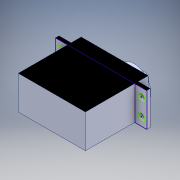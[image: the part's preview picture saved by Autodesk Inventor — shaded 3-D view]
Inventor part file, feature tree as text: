
AUTODESK INVENTOR PART (.ipt)
format: ipt  version: 2018 (Build 220112000, 112)  size: 154,624 bytes
history: native  units: mm
features: sketch x1, other x1
ambient origin geometry x8: Origin, YZ Plane, XZ Plane, XY Plane, X Axis, Y Axis, Z Axis, Center Point
bodies: Solid1 (feature_tree)
feature tree (2):
  sketch  "Sketch7"
  other  "Saliente-Extruir6"
